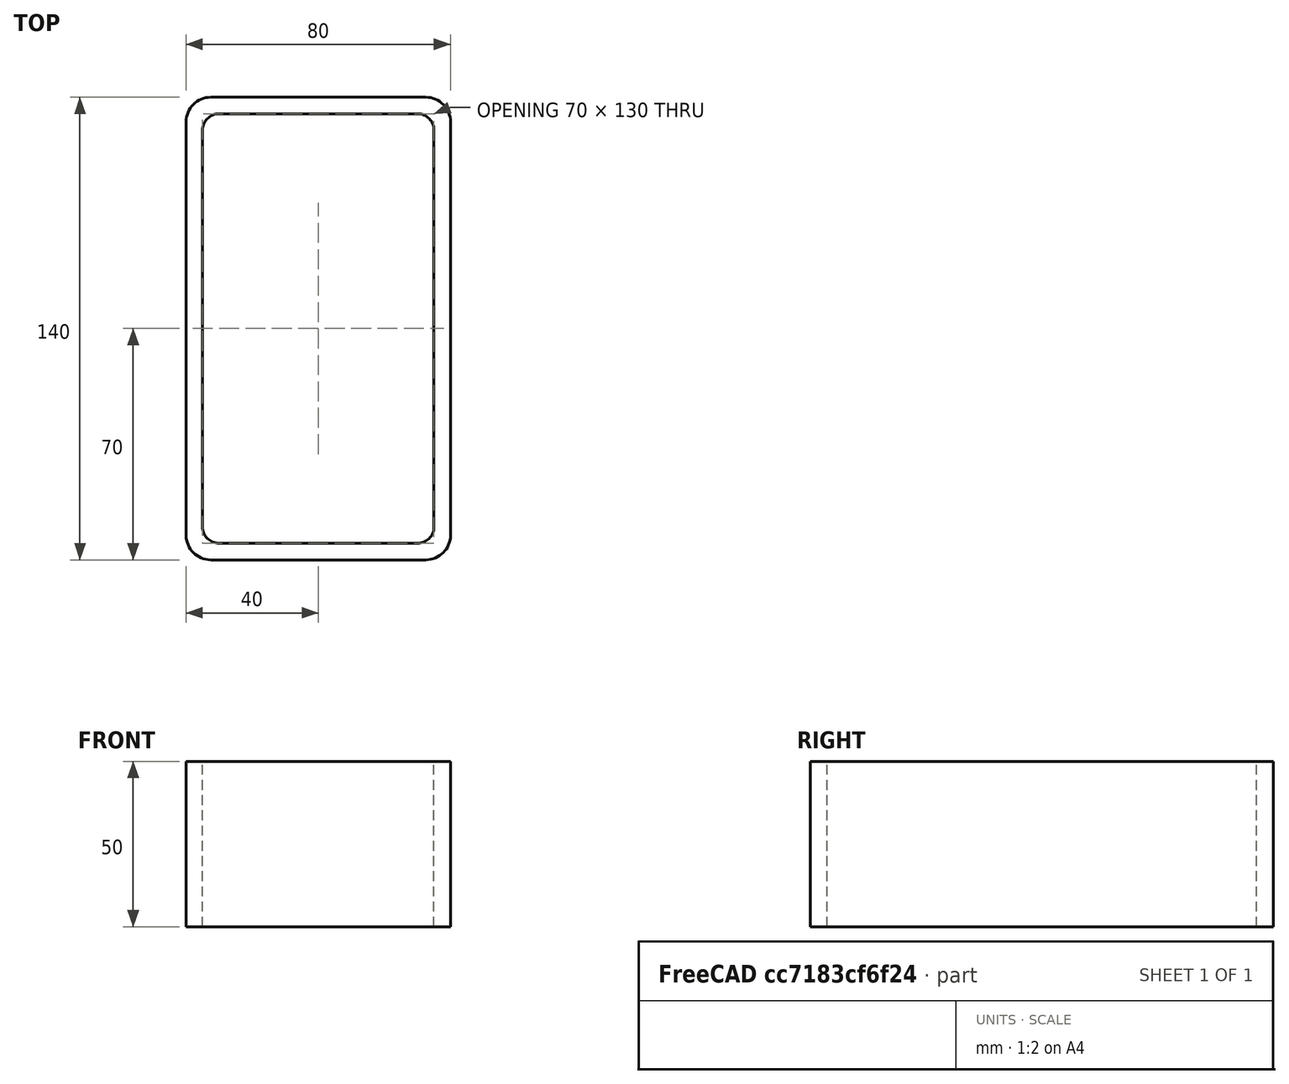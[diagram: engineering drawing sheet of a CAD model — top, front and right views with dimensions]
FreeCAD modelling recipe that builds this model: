
FCSTD DOCUMENT  (FreeCAD 0.15R4671 (Git))
Label: Rectangular hollow section 140x80x5 EN10219 S235JRH
License: All rights reserved
LicenseURL: http://en.wikipedia.org/wiki/All_rights_reserved
objects: Sketcher::SketchObject×1, Part::Extrusion×1
note: 2 computed .brp shape members not serialized (recipe doc carries the construction recipe); baked Part::Feature solids carry a one-line shape summary decoded from their .brp

FEATURE [Sketcher::SketchObject] Sketch
  sketch-geometry (16):
    g0: LineSegment StartX=-30 StartY=65 StartZ=0 EndX=30 EndY=65 EndZ=0
    g1: LineSegment StartX=35 StartY=60 StartZ=0 EndX=35 EndY=-60 EndZ=0
    g2: LineSegment StartX=30 StartY=-65 StartZ=0 EndX=-30 EndY=-65 EndZ=0
    g3: LineSegment StartX=-35 StartY=-60 StartZ=0 EndX=-35 EndY=60 EndZ=0
    g4: LineSegment StartX=-32.5 StartY=70 StartZ=0 EndX=32.5 EndY=70 EndZ=0
    g5: LineSegment StartX=40 StartY=62.5 StartZ=0 EndX=40 EndY=-62.5 EndZ=0
    g6: LineSegment StartX=32.5 StartY=-70 StartZ=0 EndX=-32.5 EndY=-70 EndZ=0
    g7: LineSegment StartX=-40 StartY=-62.5 StartZ=0 EndX=-40 EndY=62.5 EndZ=0
    g8: ArcOfCircle CenterX=-30 CenterY=60 CenterZ=0 NormalX=0 NormalY=0 NormalZ=1 Radius=5 StartAngle=1.5708 EndAngle=3.14159
    g9: ArcOfCircle CenterX=30 CenterY=60 CenterZ=0 NormalX=0 NormalY=0 NormalZ=1 Radius=5 StartAngle=0 EndAngle=1.5708
    g10: ArcOfCircle CenterX=30 CenterY=-60 CenterZ=0 NormalX=0 NormalY=0 NormalZ=1 Radius=5 StartAngle=4.71239 EndAngle=6.28319
    g11: ArcOfCircle CenterX=-30 CenterY=-60 CenterZ=0 NormalX=0 NormalY=0 NormalZ=1 Radius=5 StartAngle=3.14159 EndAngle=4.71239
    g12: ArcOfCircle CenterX=32.5 CenterY=62.5 CenterZ=0 NormalX=0 NormalY=0 NormalZ=1 Radius=7.5 StartAngle=0 EndAngle=1.5708
    g13: ArcOfCircle CenterX=32.5 CenterY=-62.5 CenterZ=0 NormalX=0 NormalY=0 NormalZ=1 Radius=7.5 StartAngle=4.71239 EndAngle=6.28319
    g14: ArcOfCircle CenterX=-32.5 CenterY=-62.5 CenterZ=0 NormalX=0 NormalY=0 NormalZ=1 Radius=7.5 StartAngle=3.14159 EndAngle=4.71239
    g15: ArcOfCircle CenterX=-32.5 CenterY=62.5 CenterZ=0 NormalX=0 NormalY=0 NormalZ=1 Radius=7.5 StartAngle=1.5708 EndAngle=3.14159
  constraints (36):
    c: Horizontal(g2)
    c: Vertical(g3)
    c: Horizontal(g6)
    c: Vertical(g7)
    c: Tangent(g3,g8) = 1.5708
    c: Tangent(g0,g8) = 1.5708
    c: Tangent(g0,g9) = 1.5708
    c: Tangent(g1,g9) = 1.5708
    c: Tangent(g1,g10) = 1.5708
    c: Tangent(g2,g10) = 1.5708
    c: Tangent(g2,g11) = 1.5708
    c: Tangent(g3,g11) = 1.5708
    c: Tangent(g4,g12) = 1.5708
    c: Tangent(g5,g12) = 1.5708
    c: Tangent(g5,g13) = 1.5708
    c: Tangent(g6,g13) = 1.5708
    c: Tangent(g6,g14) = 1.5708
    c: Tangent(g7,g14) = 1.5708
    c: Tangent(g7,g15) = 1.5708
    c: Tangent(g4,g15) = 1.5708
    c: Equal(g9,g8)
    c: Equal(g9,g11)
    c: Equal(g9,g10)
    c: Equal(g12,g15)
    c: Equal(g12,g14)
    c: Equal(g12,g13)
    c: Symmetric(g4,g6,g-1)
    c: Symmetric(g7,g5,g-2)
    c: DistanceY(g4,g6) = -140
    c: DistanceX(g7,g5) = 80
    c: Symmetric(g3,g1,g-2)
    c: Symmetric(g0,g2,g-1)
    c: DistanceY(g0,g4) = 5
    c: DistanceX(g5,g1) = -5
    c: Radius(g9) = 5
    c: Radius(g12) = 7.5
FEATURE [Part::Extrusion] Extrude  label="Rectangular hollow section 140x80x5 EN10219 S235JRH"
  Base = -> Sketch
  Dir = (0,0,50)
  Solid = true
